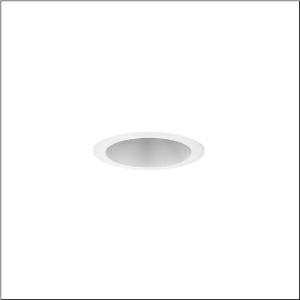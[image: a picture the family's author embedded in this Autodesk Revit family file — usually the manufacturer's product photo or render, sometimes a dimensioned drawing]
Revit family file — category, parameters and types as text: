
# Revit family: lunis_31_mini_51dn157e31
name_source: partatom
category: Lighting Fixtures
units: mm (PartAtom-declared; Revit-internal decimal feet)

## family parameters
Cut with Voids When Loaded = No
Host = Face
Light Source = No
Part Type = Normal
Room Calculation Point = No
Round Connector Dimension = Use Diameter
Shared = No

## types (1)
- Lunis 31 mini (1 x LED, 1000 lm, 8.3 W, 3000K)
    Apparent Load = 8 VA
    CIE Flux Codes = 93 98 100 100 100
    Color Rendering = 80
    Color Temperature = 3000K
    Default Elevation = 1800 mm
    Description = Lunis 31,  mini, downlight, light control with lens, light emission: direct distribution, LED rated luminous flux: 1.000lm, light colour: 830, mains connection: 220..240V, AC, 50/60Hz, housing, white, protection rating (complete): IP20, protection rating (on room side): IP54, insulation class (complete): insulation class II (safety insulation), certification: CE, packaging unit: 1 piece
    Height = 0 mm  [stored 0 ft]
    Lamp = 1 x LED
    Lamp Light Flux = 1000 lm
    Lamp Power = 8.3 W
    Lamp count = 1
    Length = 188 mm  [stored 0.616798 ft]
    Luminous efficacy = 120 lm/W
    Manufacturer = Siteco
    ModVariant = No
    Model = 51DN157E31
    Mounting Place = Ceiling
    Mounting Type = Recessed
    Number of Poles = 1
    OnlyDefault = Yes
    Power Factor = 1
    Product Name = Lunis 31 mini
    Product group = downlight
    ProductGroupID = 400
    Protection Class = Protection class II
    Protection Degree = IP 20
    RLX_Detail_Level = 1
    RLX_Emergency_Light_Flux = 0 lm
    RLX_Emergency_Type = 0
    RLX_Emergency_Type_DB = No
    RlxData = <blob elided: 21797 chars, md5=09af836f>
    Socket = socket
    Standby Power = 0 W
    System Light Flux = 1000 lm
    System Power = 8 W
    Type Comments = Product without accessories
    Type Image = l_1005624.jpg
    URL = http://relux.com
    VarID = ---
    Voltage = 0 V
    Weight = 0.00 kg
    Width = 0 mm  [stored 0 ft]

note: [stored X ft] marks values corroborated as IEEE doubles in the binary element streams (Revit-internal decimal feet)

## geometry (parser evidence)
native form markers: Blend x4, Sweep x11
no freeform markers — native parametric forms only
